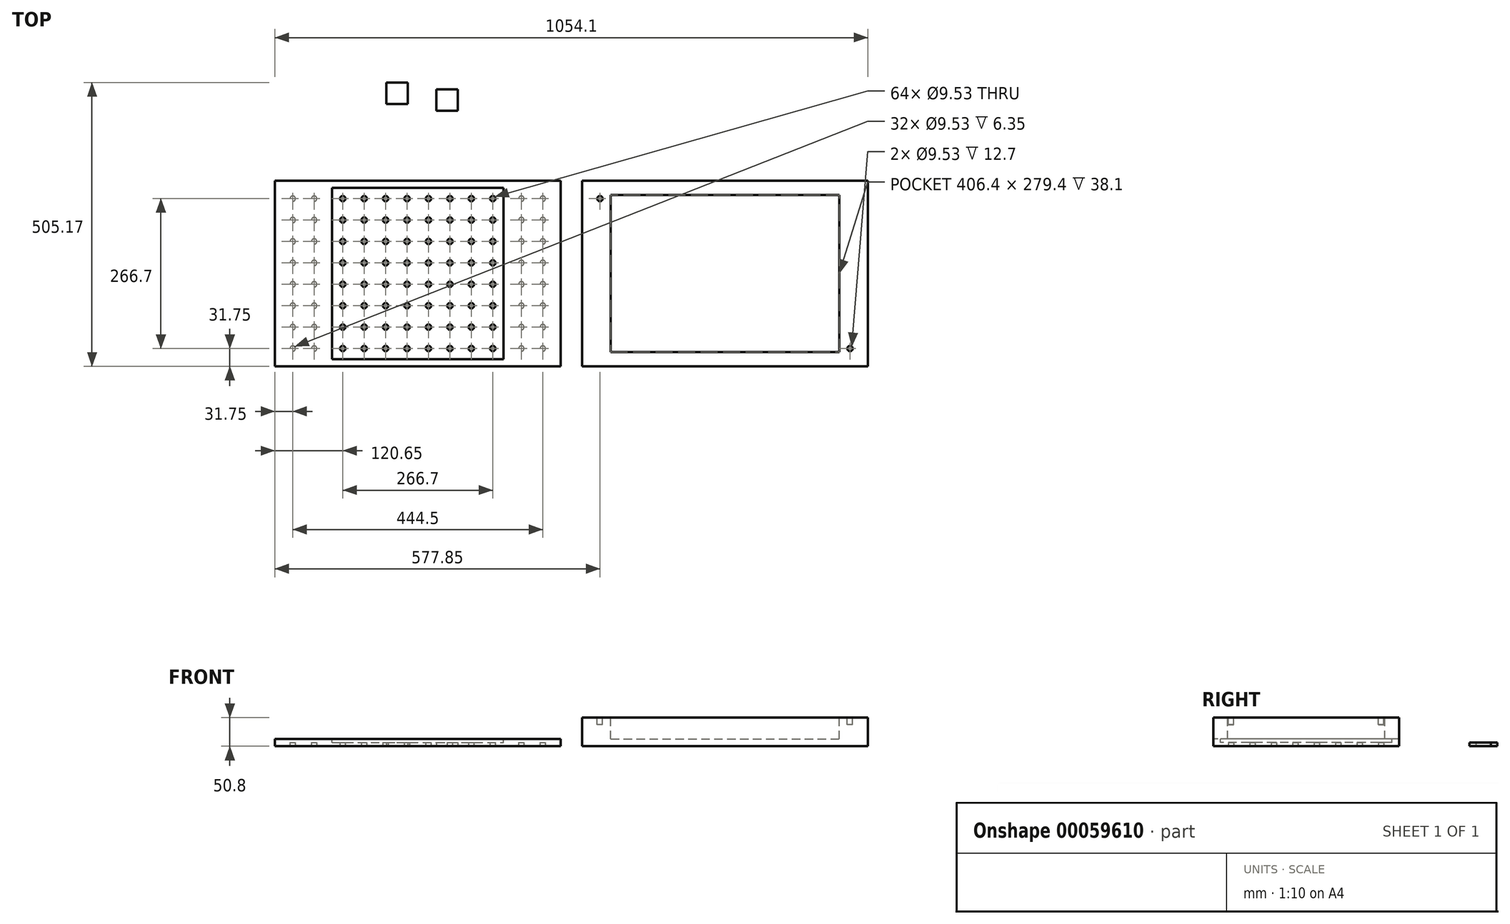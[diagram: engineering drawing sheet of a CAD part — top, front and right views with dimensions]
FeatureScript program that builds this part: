
annotation { "Feature Type Name" : "Feature", "Feature Type Description" : "" }
export const myFeature = defineFeature(function(context is Context, id is Id, definition is map)
    precondition{}
    {
        {
            var Q0;
            Q0=qCreatedBy(makeId("Top.planeOp"),FACE);
            var sketch = newSketch(context, id + "F0", { "sketchPlane" : qUnion([Q0])});
            skLineSegment(sketch, "E0.bottom", {"start": v(-508, 0) * mm, "end": v(0, 0) * mm});
            skLineSegment(sketch, "E0.top", {"start": v(-508, -330.2) * mm, "end": v(0, -330.2) * mm});
            skLineSegment(sketch, "E0.left", {"start": v(-508, 0) * mm, "end": v(-508, -330.2) * mm});
            skLineSegment(sketch, "E0.right", {"start": v(0, 0) * mm, "end": v(0, -330.2) * mm});
            skSolve(sketch);
        }
        {
            var Q0;
            Q0 = qSketchRegion(id + "F0", true);
            var Q1;
            Q1=makeQuery(id+"F0.imprint","IMPRINT",FACE,{"disambiguationData":[TD([[makeQuery(id+"F0.imprint","IMPRINT",EDGE,{"derivedFrom":sQuery(id+"F0.wireOp",EDGE,"E0.bottom")}),-1.0]])]});
            extrude(context, id + "F1", {"entities" : qUnion([Q0, Q1]), "depth" : 12.7 * mm});
        }
        {
            var Q0;
            Q0=makeQuery(id+"F1.opExtrude","CAP_FACE",FACE,{"disambiguationData":[OSD([sQuery(id+"F0.wireOp",EDGE,"E0.bottom"),sQuery(id+"F0.wireOp",EDGE,"E0.top"),sQuery(id+"F0.wireOp",EDGE,"E0.left"),sQuery(id+"F0.wireOp",EDGE,"E0.right")])],"isStart":true});
            var sketch = newSketch(context, id + "F2", { "sketchPlane" : qUnion([Q0])});
            skLineSegment(sketch, "E1.bottom", {"start": v(-406.4, 317.5) * mm, "end": v(-101.6, 317.5) * mm});
            skLineSegment(sketch, "E1.top", {"start": v(-406.4, 12.7) * mm, "end": v(-101.6, 12.7) * mm});
            skLineSegment(sketch, "E1.left", {"start": v(-406.4, 317.5) * mm, "end": v(-406.4, 12.7) * mm});
            skLineSegment(sketch, "E1.right", {"start": v(-101.6, 317.5) * mm, "end": v(-101.6, 12.7) * mm});
            skLineSegment(sketch, "E2.bottom", {"start": v(-495.3, 12.7) * mm, "end": v(-419.1, 12.7) * mm});
            skLineSegment(sketch, "E2.top", {"start": v(-495.3, 317.5) * mm, "end": v(-419.1, 317.5) * mm});
            skLineSegment(sketch, "E2.left", {"start": v(-495.3, 12.7) * mm, "end": v(-495.3, 317.5) * mm});
            skLineSegment(sketch, "E2.right", {"start": v(-419.1, 12.7) * mm, "end": v(-419.1, 317.5) * mm});
            skLineSegment(sketch, "E3.bottom", {"start": v(-88.9, 317.5) * mm, "end": v(-12.7, 317.5) * mm});
            skLineSegment(sketch, "E3.top", {"start": v(-88.9, 12.7) * mm, "end": v(-12.7, 12.7) * mm});
            skLineSegment(sketch, "E3.left", {"start": v(-88.9, 317.5) * mm, "end": v(-88.9, 12.7) * mm});
            skLineSegment(sketch, "E3.right", {"start": v(-12.7, 317.5) * mm, "end": v(-12.7, 12.7) * mm});
            skSolve(sketch);
        }
        {
            var Q0;
            Q0=makeQuery(id+"F2.imprint","IMPRINT",FACE,{"disambiguationData":[TD([[makeQuery(id+"F2.imprint","IMPRINT",EDGE,{"derivedFrom":sQuery(id+"F2.wireOp",EDGE,"E1.bottom")}),1.0]])]});
            var sketch = newSketch(context, id + "F3", { "sketchPlane" : qUnion([Q0])});
            skCircle(sketch, "E4", {"center": v(-476.25, 298.45) * mm, "radius": 4.76 * mm});
            skCircle(sketch, "E5", {"center": v(-387.35, 298.45) * mm, "radius": 4.76 * mm});
            skCircle(sketch, "E6", {"center": v(-31.75, 298.45) * mm, "radius": 4.76 * mm});
            skCircle(sketch, "E7.0.1.0", {"center": v(-476.25, 260.35) * mm, "radius": 4.76 * mm});
            skCircle(sketch, "E7.0.2.0", {"center": v(-476.25, 222.25) * mm, "radius": 4.76 * mm});
            skCircle(sketch, "E7.0.3.0", {"center": v(-476.25, 184.15) * mm, "radius": 4.76 * mm});
            skCircle(sketch, "E7.0.4.0", {"center": v(-476.25, 146.05) * mm, "radius": 4.76 * mm});
            skCircle(sketch, "E7.0.5.0", {"center": v(-476.25, 107.95) * mm, "radius": 4.76 * mm});
            skCircle(sketch, "E7.0.6.0", {"center": v(-476.25, 69.85) * mm, "radius": 4.76 * mm});
            skCircle(sketch, "E7.0.7.0", {"center": v(-476.25, 31.75) * mm, "radius": 4.76 * mm});
            skCircle(sketch, "E7.1.0.0", {"center": v(-438.15, 298.45) * mm, "radius": 4.76 * mm});
            skCircle(sketch, "E7.1.1.0", {"center": v(-438.15, 260.35) * mm, "radius": 4.76 * mm});
            skCircle(sketch, "E7.1.2.0", {"center": v(-438.15, 222.25) * mm, "radius": 4.76 * mm});
            skCircle(sketch, "E7.1.3.0", {"center": v(-438.15, 184.15) * mm, "radius": 4.76 * mm});
            skCircle(sketch, "E7.1.4.0", {"center": v(-438.15, 146.05) * mm, "radius": 4.76 * mm});
            skCircle(sketch, "E7.1.5.0", {"center": v(-438.15, 107.95) * mm, "radius": 4.76 * mm});
            skCircle(sketch, "E7.1.6.0", {"center": v(-438.15, 69.85) * mm, "radius": 4.76 * mm});
            skCircle(sketch, "E7.1.7.0", {"center": v(-438.15, 31.75) * mm, "radius": 4.76 * mm});
            skLineSegment(sketch, "E7.direction1", {"start": v(-476.25, 298.45) * mm, "end": v(-438.15, 298.45) * mm, "construction": true});
            skLineSegment(sketch, "E7.direction2", {"start": v(-476.25, 298.45) * mm, "end": v(-476.25, 260.35) * mm, "construction": true});
            skCircle(sketch, "E8.0.1.0", {"center": v(-387.35, 260.35) * mm, "radius": 4.76 * mm});
            skCircle(sketch, "E8.0.2.0", {"center": v(-387.35, 222.25) * mm, "radius": 4.76 * mm});
            skCircle(sketch, "E8.0.3.0", {"center": v(-387.35, 184.15) * mm, "radius": 4.76 * mm});
            skCircle(sketch, "E8.0.4.0", {"center": v(-387.35, 146.05) * mm, "radius": 4.76 * mm});
            skCircle(sketch, "E8.0.5.0", {"center": v(-387.35, 107.95) * mm, "radius": 4.76 * mm});
            skCircle(sketch, "E8.0.6.0", {"center": v(-387.35, 69.85) * mm, "radius": 4.76 * mm});
            skCircle(sketch, "E8.0.7.0", {"center": v(-387.35, 31.75) * mm, "radius": 4.76 * mm});
            skCircle(sketch, "E8.1.0.0", {"center": v(-349.25, 298.45) * mm, "radius": 4.76 * mm});
            skCircle(sketch, "E8.1.1.0", {"center": v(-349.25, 260.35) * mm, "radius": 4.76 * mm});
            skCircle(sketch, "E8.1.2.0", {"center": v(-349.25, 222.25) * mm, "radius": 4.76 * mm});
            skCircle(sketch, "E8.1.3.0", {"center": v(-349.25, 184.15) * mm, "radius": 4.76 * mm});
            skCircle(sketch, "E8.1.4.0", {"center": v(-349.25, 146.05) * mm, "radius": 4.76 * mm});
            skCircle(sketch, "E8.1.5.0", {"center": v(-349.25, 107.95) * mm, "radius": 4.76 * mm});
            skCircle(sketch, "E8.1.6.0", {"center": v(-349.25, 69.85) * mm, "radius": 4.76 * mm});
            skCircle(sketch, "E8.1.7.0", {"center": v(-349.25, 31.75) * mm, "radius": 4.76 * mm});
            skCircle(sketch, "E8.2.0.0", {"center": v(-311.15, 298.45) * mm, "radius": 4.76 * mm});
            skCircle(sketch, "E8.2.1.0", {"center": v(-311.15, 260.35) * mm, "radius": 4.76 * mm});
            skCircle(sketch, "E8.2.2.0", {"center": v(-311.15, 222.25) * mm, "radius": 4.76 * mm});
            skCircle(sketch, "E8.2.3.0", {"center": v(-311.15, 184.15) * mm, "radius": 4.76 * mm});
            skCircle(sketch, "E8.2.4.0", {"center": v(-311.15, 146.05) * mm, "radius": 4.76 * mm});
            skCircle(sketch, "E8.2.5.0", {"center": v(-311.15, 107.95) * mm, "radius": 4.76 * mm});
            skCircle(sketch, "E8.2.6.0", {"center": v(-311.15, 69.85) * mm, "radius": 4.76 * mm});
            skCircle(sketch, "E8.2.7.0", {"center": v(-311.15, 31.75) * mm, "radius": 4.76 * mm});
            skCircle(sketch, "E8.3.0.0", {"center": v(-273.05, 298.45) * mm, "radius": 4.76 * mm});
            skCircle(sketch, "E8.3.1.0", {"center": v(-273.05, 260.35) * mm, "radius": 4.76 * mm});
            skCircle(sketch, "E8.3.2.0", {"center": v(-273.05, 222.25) * mm, "radius": 4.76 * mm});
            skCircle(sketch, "E8.3.3.0", {"center": v(-273.05, 184.15) * mm, "radius": 4.76 * mm});
            skCircle(sketch, "E8.3.4.0", {"center": v(-273.05, 146.05) * mm, "radius": 4.76 * mm});
            skCircle(sketch, "E8.3.5.0", {"center": v(-273.05, 107.95) * mm, "radius": 4.76 * mm});
            skCircle(sketch, "E8.3.6.0", {"center": v(-273.05, 69.85) * mm, "radius": 4.76 * mm});
            skCircle(sketch, "E8.3.7.0", {"center": v(-273.05, 31.75) * mm, "radius": 4.76 * mm});
            skCircle(sketch, "E8.4.0.0", {"center": v(-234.95, 298.45) * mm, "radius": 4.76 * mm});
            skCircle(sketch, "E8.4.1.0", {"center": v(-234.95, 260.35) * mm, "radius": 4.76 * mm});
            skCircle(sketch, "E8.4.2.0", {"center": v(-234.95, 222.25) * mm, "radius": 4.76 * mm});
            skCircle(sketch, "E8.4.3.0", {"center": v(-234.95, 184.15) * mm, "radius": 4.76 * mm});
            skCircle(sketch, "E8.4.4.0", {"center": v(-234.95, 146.05) * mm, "radius": 4.76 * mm});
            skCircle(sketch, "E8.4.5.0", {"center": v(-234.95, 107.95) * mm, "radius": 4.76 * mm});
            skCircle(sketch, "E8.4.6.0", {"center": v(-234.95, 69.85) * mm, "radius": 4.76 * mm});
            skCircle(sketch, "E8.4.7.0", {"center": v(-234.95, 31.75) * mm, "radius": 4.76 * mm});
            skCircle(sketch, "E8.5.0.0", {"center": v(-196.85, 298.45) * mm, "radius": 4.76 * mm});
            skCircle(sketch, "E8.5.1.0", {"center": v(-196.85, 260.35) * mm, "radius": 4.76 * mm});
            skCircle(sketch, "E8.5.2.0", {"center": v(-196.85, 222.25) * mm, "radius": 4.76 * mm});
            skCircle(sketch, "E8.5.3.0", {"center": v(-196.85, 184.15) * mm, "radius": 4.76 * mm});
            skCircle(sketch, "E8.5.4.0", {"center": v(-196.85, 146.05) * mm, "radius": 4.76 * mm});
            skCircle(sketch, "E8.5.5.0", {"center": v(-196.85, 107.95) * mm, "radius": 4.76 * mm});
            skCircle(sketch, "E8.5.6.0", {"center": v(-196.85, 69.85) * mm, "radius": 4.76 * mm});
            skCircle(sketch, "E8.5.7.0", {"center": v(-196.85, 31.75) * mm, "radius": 4.76 * mm});
            skCircle(sketch, "E8.6.0.0", {"center": v(-158.75, 298.45) * mm, "radius": 4.76 * mm});
            skCircle(sketch, "E8.6.1.0", {"center": v(-158.75, 260.35) * mm, "radius": 4.76 * mm});
            skCircle(sketch, "E8.6.2.0", {"center": v(-158.75, 222.25) * mm, "radius": 4.76 * mm});
            skCircle(sketch, "E8.6.3.0", {"center": v(-158.75, 184.15) * mm, "radius": 4.76 * mm});
            skCircle(sketch, "E8.6.4.0", {"center": v(-158.75, 146.05) * mm, "radius": 4.76 * mm});
            skCircle(sketch, "E8.6.5.0", {"center": v(-158.75, 107.95) * mm, "radius": 4.76 * mm});
            skCircle(sketch, "E8.6.6.0", {"center": v(-158.75, 69.85) * mm, "radius": 4.76 * mm});
            skCircle(sketch, "E8.6.7.0", {"center": v(-158.75, 31.75) * mm, "radius": 4.76 * mm});
            skCircle(sketch, "E8.7.0.0", {"center": v(-120.65, 298.45) * mm, "radius": 4.76 * mm});
            skCircle(sketch, "E8.7.1.0", {"center": v(-120.65, 260.35) * mm, "radius": 4.76 * mm});
            skCircle(sketch, "E8.7.2.0", {"center": v(-120.65, 222.25) * mm, "radius": 4.76 * mm});
            skCircle(sketch, "E8.7.3.0", {"center": v(-120.65, 184.15) * mm, "radius": 4.76 * mm});
            skCircle(sketch, "E8.7.4.0", {"center": v(-120.65, 146.05) * mm, "radius": 4.76 * mm});
            skCircle(sketch, "E8.7.5.0", {"center": v(-120.65, 107.95) * mm, "radius": 4.76 * mm});
            skCircle(sketch, "E8.7.6.0", {"center": v(-120.65, 69.85) * mm, "radius": 4.76 * mm});
            skCircle(sketch, "E8.7.7.0", {"center": v(-120.65, 31.75) * mm, "radius": 4.76 * mm});
            skLineSegment(sketch, "E8.direction1", {"start": v(-387.35, 298.45) * mm, "end": v(-349.25, 298.45) * mm, "construction": true});
            skLineSegment(sketch, "E8.direction2", {"start": v(-387.35, 298.45) * mm, "end": v(-387.35, 260.35) * mm, "construction": true});
            skCircle(sketch, "E9.0.1.0", {"center": v(-31.75, 260.35) * mm, "radius": 4.76 * mm});
            skCircle(sketch, "E9.0.2.0", {"center": v(-31.75, 222.25) * mm, "radius": 4.76 * mm});
            skCircle(sketch, "E9.0.3.0", {"center": v(-31.75, 184.15) * mm, "radius": 4.76 * mm});
            skCircle(sketch, "E9.0.4.0", {"center": v(-31.75, 146.05) * mm, "radius": 4.76 * mm});
            skCircle(sketch, "E9.0.5.0", {"center": v(-31.75, 107.95) * mm, "radius": 4.76 * mm});
            skCircle(sketch, "E9.0.6.0", {"center": v(-31.75, 69.85) * mm, "radius": 4.76 * mm});
            skCircle(sketch, "E9.0.7.0", {"center": v(-31.75, 31.75) * mm, "radius": 4.76 * mm});
            skCircle(sketch, "E9.1.0.0", {"center": v(-69.85, 298.45) * mm, "radius": 4.76 * mm});
            skCircle(sketch, "E9.1.1.0", {"center": v(-69.85, 260.35) * mm, "radius": 4.76 * mm});
            skCircle(sketch, "E9.1.2.0", {"center": v(-69.85, 222.25) * mm, "radius": 4.76 * mm});
            skCircle(sketch, "E9.1.3.0", {"center": v(-69.85, 184.15) * mm, "radius": 4.76 * mm});
            skCircle(sketch, "E9.1.4.0", {"center": v(-69.85, 146.05) * mm, "radius": 4.76 * mm});
            skCircle(sketch, "E9.1.5.0", {"center": v(-69.85, 107.95) * mm, "radius": 4.76 * mm});
            skCircle(sketch, "E9.1.6.0", {"center": v(-69.85, 69.85) * mm, "radius": 4.76 * mm});
            skCircle(sketch, "E9.1.7.0", {"center": v(-69.85, 31.75) * mm, "radius": 4.76 * mm});
            skLineSegment(sketch, "E9.direction1", {"start": v(-31.75, 298.45) * mm, "end": v(-69.85, 298.45) * mm, "construction": true});
            skLineSegment(sketch, "E9.direction2", {"start": v(-31.75, 298.45) * mm, "end": v(-31.75, 260.35) * mm, "construction": true});
            skSolve(sketch);
        }
        {
            var Q0;
            Q0 = qSketchRegion(id + "F3", true);
            extrude(context, id + "F4", {"entities" : qUnion([Q0]), "operationType" : NewBodyOperationType.REMOVE, "oppositeDirection" : true, "depth" : 6.35 * mm});
        }
        {
            var Q0;
            Q0=qCreatedBy(makeId("Top.planeOp"),FACE);
            var sketch = newSketch(context, id + "F5", { "sketchPlane" : qUnion([Q0])});
            skLineSegment(sketch, "E10.bottom", {"start": v(38.1, 0) * mm, "end": v(546.1, 0) * mm});
            skLineSegment(sketch, "E10.top", {"start": v(38.1, -330.2) * mm, "end": v(546.1, -330.2) * mm});
            skLineSegment(sketch, "E10.left", {"start": v(38.1, 0) * mm, "end": v(38.1, -330.2) * mm});
            skLineSegment(sketch, "E10.right", {"start": v(546.1, 0) * mm, "end": v(546.1, -330.2) * mm});
            skSolve(sketch);
        }
        {
            var Q0;
            Q0 = qSketchRegion(id + "F5", true);
            extrude(context, id + "F6", {"entities" : qUnion([Q0]), "depth" : 50.8 * mm});
        }
        {
            var Q0;
            Q0=makeQuery(id+"F6.opExtrude","CAP_FACE",FACE,{"disambiguationData":[OSD([sQuery(id+"F5.wireOp",EDGE,"E10.bottom"),sQuery(id+"F5.wireOp",EDGE,"E10.top"),sQuery(id+"F5.wireOp",EDGE,"E10.left"),sQuery(id+"F5.wireOp",EDGE,"E10.right")])],"isStart":false});
            var sketch = newSketch(context, id + "F7", { "sketchPlane" : qUnion([Q0])});
            skLineSegment(sketch, "E11.bottom", {"start": v(88.9, -25.4) * mm, "end": v(495.3, -25.4) * mm});
            skLineSegment(sketch, "E11.top", {"start": v(88.9, -304.8) * mm, "end": v(495.3, -304.8) * mm});
            skLineSegment(sketch, "E11.left", {"start": v(88.9, -25.4) * mm, "end": v(88.9, -304.8) * mm});
            skLineSegment(sketch, "E11.right", {"start": v(495.3, -25.4) * mm, "end": v(495.3, -304.8) * mm});
            skSolve(sketch);
        }
        {
            var Q0;
            Q0 = qSketchRegion(id + "F7", true);
            extrude(context, id + "F8", {"entities" : qUnion([Q0]), "operationType" : NewBodyOperationType.REMOVE, "oppositeDirection" : true, "depth" : 38.1 * mm});
        }
        {
            var Q0;
            Q0=makeQuery(id+"F6.opExtrude","CAP_FACE",FACE,{"disambiguationData":[OSD([sQuery(id+"F5.wireOp",EDGE,"E10.bottom"),sQuery(id+"F5.wireOp",EDGE,"E10.top"),sQuery(id+"F5.wireOp",EDGE,"E10.left"),sQuery(id+"F5.wireOp",EDGE,"E10.right")])],"isStart":false});
            var sketch = newSketch(context, id + "F9", { "sketchPlane" : qUnion([Q0])});
            skCircle(sketch, "E12", {"center": v(69.85, -31.75) * mm, "radius": 4.76 * mm});
            skCircle(sketch, "E13", {"center": v(514.35, -298.45) * mm, "radius": 4.76 * mm});
            skSolve(sketch);
        }
        {
            var Q0;
            Q0 = qSketchRegion(id + "F9", true);
            extrude(context, id + "F10", {"entities" : qUnion([Q0]), "operationType" : NewBodyOperationType.REMOVE, "oppositeDirection" : true, "depth" : 12.7 * mm});
        }
        {
            var Q0;
            Q0=qCreatedBy(makeId("Top.planeOp"),FACE);
            var sketch = newSketch(context, id + "F11", { "sketchPlane" : qUnion([Q0])});
            skLineSegment(sketch, "E14.bottom", {"start": v(-309.66, 174.97) * mm, "end": v(-271.56, 174.97) * mm});
            skLineSegment(sketch, "E14.top", {"start": v(-309.66, 136.87) * mm, "end": v(-271.56, 136.87) * mm});
            skLineSegment(sketch, "E14.left", {"start": v(-309.66, 174.97) * mm, "end": v(-309.66, 136.87) * mm});
            skLineSegment(sketch, "E14.right", {"start": v(-271.56, 174.97) * mm, "end": v(-271.56, 136.87) * mm});
            skSolve(sketch);
        }
        {
            var Q0;
            Q0=qCreatedBy(makeId("Top.planeOp"),FACE);
            var sketch = newSketch(context, id + "F12", { "sketchPlane" : qUnion([Q0])});
            skLineSegment(sketch, "E15.bottom", {"start": v(-220.97, 162.93) * mm, "end": v(-182.87, 162.93) * mm});
            skLineSegment(sketch, "E15.top", {"start": v(-220.97, 124.83) * mm, "end": v(-182.87, 124.83) * mm});
            skLineSegment(sketch, "E15.left", {"start": v(-220.97, 162.93) * mm, "end": v(-220.97, 124.83) * mm});
            skLineSegment(sketch, "E15.right", {"start": v(-182.87, 162.93) * mm, "end": v(-182.87, 124.83) * mm});
            skSolve(sketch);
        }
        {
            var Q0;
            Q0 = qSketchRegion(id + "F11", true);
            extrude(context, id + "F13", {"entities" : qUnion([Q0]), "depth" : 6.35 * mm});
        }
        {
            var Q0;
            Q0 = qSketchRegion(id + "F12", true);
            extrude(context, id + "F14", {"entities" : qUnion([Q0]), "depth" : 6.35 * mm});
        }
        {
            var Q0;
            Q0=makeQuery(id+"F1.opExtrude","CAP_FACE",FACE,{"disambiguationData":[OSD([sQuery(id+"F0.wireOp",EDGE,"E0.bottom"),sQuery(id+"F0.wireOp",EDGE,"E0.top"),sQuery(id+"F0.wireOp",EDGE,"E0.left"),sQuery(id+"F0.wireOp",EDGE,"E0.right")])],"isStart":false});
            var sketch = newSketch(context, id + "F15", { "sketchPlane" : qUnion([Q0])});
            skLineSegment(sketch, "E16.bottom", {"start": v(-406.4, -12.7) * mm, "end": v(-101.6, -12.7) * mm});
            skLineSegment(sketch, "E16.top", {"start": v(-406.4, -317.5) * mm, "end": v(-101.6, -317.5) * mm});
            skLineSegment(sketch, "E16.left", {"start": v(-406.4, -12.7) * mm, "end": v(-406.4, -317.5) * mm});
            skLineSegment(sketch, "E16.right", {"start": v(-101.6, -12.7) * mm, "end": v(-101.6, -317.5) * mm});
            skSolve(sketch);
        }
        {
            var Q0;
            Q0 = qSketchRegion(id + "F15", true);
            extrude(context, id + "F16", {"entities" : qUnion([Q0]), "operationType" : NewBodyOperationType.REMOVE, "oppositeDirection" : true, "depth" : 6.35 * mm});
        }
    });
